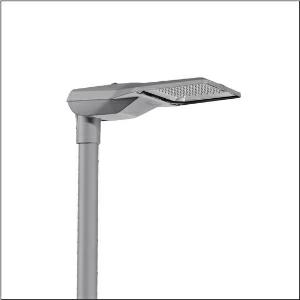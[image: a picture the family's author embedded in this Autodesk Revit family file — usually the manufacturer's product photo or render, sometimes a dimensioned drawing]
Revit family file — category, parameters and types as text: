
# Revit family: streetlight_sl_21_midi___st1_5a_5xe3p43s08lb_fbc0
name_source: partatom
category: Lighting Fixtures
units: mm (PartAtom-declared; Revit-internal decimal feet)

## family parameters
Cut with Voids When Loaded = No
Host = Face
Light Source = No
Part Type = Normal
Room Calculation Point = No
Round Connector Dimension = Use Diameter
Shared = No

## types (1)
- --- (1 x LED, 14690 lm, 98.3 W, 4000K)
    Apparent Load = 98 VA
    CIE Flux Codes = 22 53 95 100 100
    Color Rendering = 70
    Color Temperature = 4000K
    Default Elevation = 1800 mm
    Description = Streetlight SL 21 midi, mast luminaire, primary light control with lens, of PMMA, primary optical cover: cover, of toughened safety glass, transparent, light distribution: ST1.5a, light emission: direct distribution, primary light characteristic: asymmetric, installation type: side-entry, post-top, LED, High Power LED, rated luminous flux: 14.690lm, luminous efficacy: 149lm/W, light colour: 740, colour temperature: 4000K, control: overheat protection, constant luminous flux control, time-dependent luminous flux control, flexible luminous flux parameterisation, presetting dimming logarithmic, mains connection: 230..240V, AC, 50/60Hz, start of lifetime: 98W, end of service life: 101W, reduction: 45W, luminaire housing, of diecast aluminium, powder-coated, Siteco® metallic grey (DB 702S), corrosivity category C5 mid according to DIN EN ISO 12944, please order mast flange separately, inclination adjustable: 0°, 5°, 10°, 15°, sealing non-destructively replaceable, multi-level sealing system, length: 644mm, width: 335mm, height: 110mm, mast flange for spigot size: 42mm (side-entry): 5XC10008XM4, 60/48mm (side-entry/post-top): 5XC10108XM2, 76/60mm (side-entry/post-top): 5XC10108XM1, Smart Interface above, protection rating (complete): IP66, insulation class (complete): insulation class II (safety insulation), certification: CE, ENEC, ENEC+, VDE, impact resistance: IK09, permissible operating ambient temperature for outdoor applications: -40..+50°C, standard-compliant lighting for roads and squares, packaging unit: 1 piece

Light Distribution: ST1.5a
    Height = 111 mm
    Lamp = 1 x LED
    Lamp Light Flux = 14690 lm
    Lamp Power = 98.3 W
    Lamp count = 1
    Length = 644 mm
    Luminous efficacy = 149 lm/W
    Manufacturer = Siteco
    ModVariant = No
    Model = 5XE3P43S08LB
    Number of Poles = 1
    OnlyDefault = Yes
    Power Factor = 1
    Product Name = Streetlight SL 21 midi | ST1.5a
    Product group = mast luminaire | pylon top
    ProductGroupID = 6100
    Protection Class = Protection class II
    Protection Degree = IP 66
    RLX_Detail_Level = 1
    RLX_Emergency_Light_Flux = 0 lm
    RLX_Emergency_Type = 0
    RLX_Emergency_Type_DB = No
    RlxData = <blob elided: 94577 chars, md5=c37f1c6f>
    Socket = socket
    Standby Power = 0 W
    System Light Flux = 14690 lm
    System Power = 98 W
    Type Comments = factory setting: luminous flux: 100 % | dim-lin: 254 | 1020 mA
    Type Image = l_1004302.jpg
    URL = http://relux.com
    VarID = @adj_109509
    Voltage = 0 V
    Weight = 0.00 kg
    Width = 336 mm

## geometry (parser evidence)
native form markers: Blend x4, Sweep x8
no freeform markers — native parametric forms only
